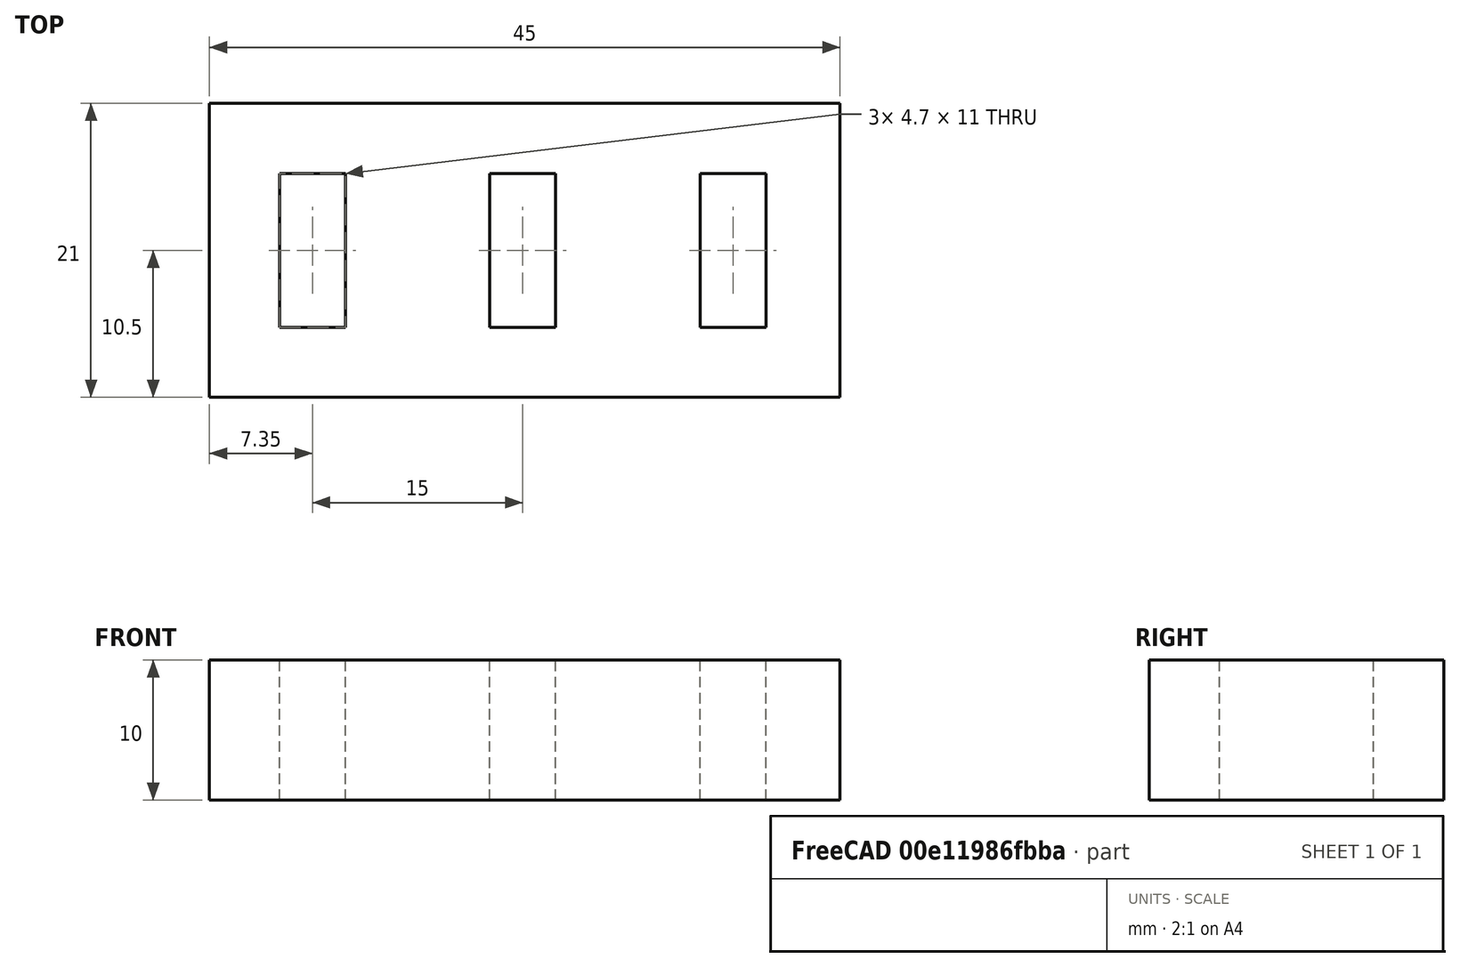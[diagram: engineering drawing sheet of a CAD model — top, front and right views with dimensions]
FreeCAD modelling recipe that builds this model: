
FCSTD DOCUMENT  (FreeCAD 0.21R33694 (Git))
Label: OJT1_T08_R01Porta-pendrives
License: All rights reserved
LicenseURL: https://en.wikipedia.org/wiki/All_rights_reserved
objects: Part::Box×4, Part::MultiFuse×1, Part::Cut×1
note: 6 computed .brp shape members not serialized (recipe doc carries the construction recipe); baked Part::Feature solids carry a one-line shape summary decoded from their .brp

FEATURE [Part::Box] Box  label="Ranura1"
  AttacherType = Attacher::AttachEngine3D
  Height = 12
  Length = 4.7
  Width = 11
FEATURE [Part::Box] Box001  label="Ranura002"
  AttacherType = Attacher::AttachEngine3D
  Height = 12
  Length = 4.7
  Placement = pos=(15,0,0) rot=(0,0,1;0rad)
  Width = 11
  expr: .Placement.Base.x = 15
FEATURE [Part::Box] Box002  label="Ranura003"
  AttacherType = Attacher::AttachEngine3D
  Height = 12
  Length = 4.7
  Placement = pos=(30,0,0) rot=(0,0,1;0rad)
  Width = 11
  expr: .Placement.Base.x = 30
FEATURE [Part::MultiFuse] Fusion  label="Ranuras"
  Placement = pos=(5,5,0) rot=(0,0,1;0rad)
  Shapes = -> [Box001,Box,Box002]
FEATURE [Part::Box] Box003  label="Base"
  AttacherType = Attacher::AttachEngine3D
  Height = 10
  Length = 45
  Width = 21
  expr: .Placement.Base.x = 5
  expr: .Placement.Base.y = 5
FEATURE [Part::Cut] Cut
  Base = -> Box003
  Tool = -> Fusion
